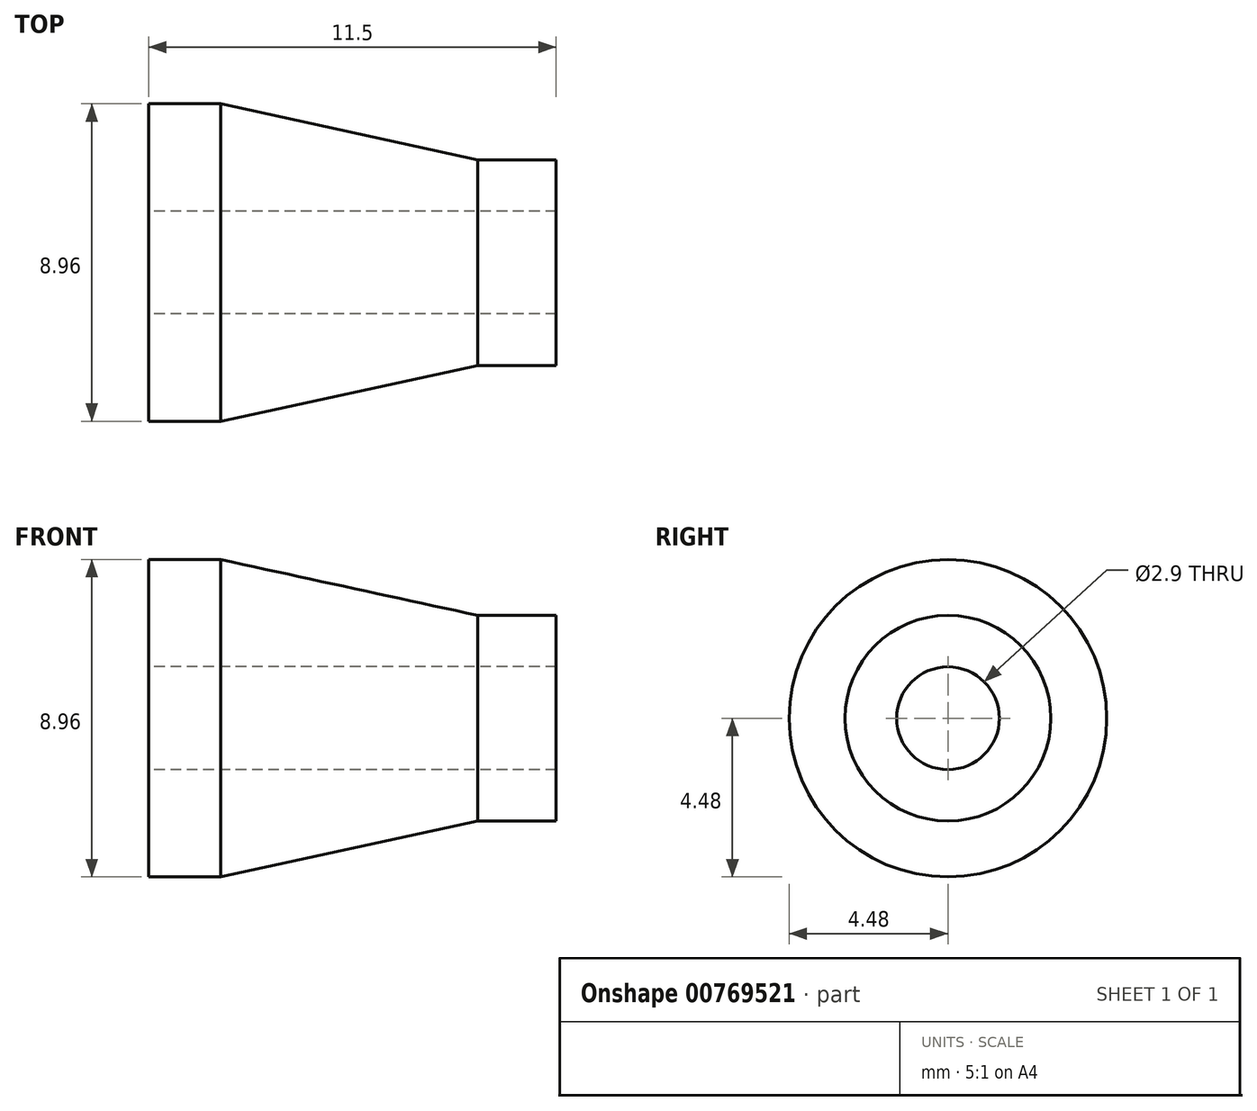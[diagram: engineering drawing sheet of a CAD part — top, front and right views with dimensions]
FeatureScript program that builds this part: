
annotation { "Feature Type Name" : "Feature", "Feature Type Description" : "" }
export const myFeature = defineFeature(function(context is Context, id is Id, definition is map)
    precondition{}
    {
        {
            var Q0;
            Q0=qCreatedBy(makeId("Front.planeOp"),FACE);
            var sketch = newSketch(context, id + "F0", { "sketchPlane" : qUnion([Q0])});
            skLineSegment(sketch, "E0", {"start": v(0, 0) * mm, "end": v(0, 4.48) * mm});
            skLineSegment(sketch, "E1", {"start": v(0, 4.48) * mm, "end": v(2.03, 4.48) * mm});
            skLineSegment(sketch, "E2", {"start": v(2.03, 4.48) * mm, "end": v(2.03, 0) * mm});
            skLineSegment(sketch, "E3", {"start": v(2.03, 4.48) * mm, "end": v(9.3, 2.9) * mm});
            skLineSegment(sketch, "E4", {"start": v(9.3, 2.9) * mm, "end": v(9.3, 0) * mm});
            skLineSegment(sketch, "E5", {"start": v(11.5, 0) * mm, "end": v(11.5, 2.9) * mm});
            skLineSegment(sketch, "E6", {"start": v(9.3, 2.9) * mm, "end": v(11.5, 2.9) * mm});
            skLineSegment(sketch, "E7.trimOffspring", {"start": v(11.5, 0) * mm, "end": v(15.36, 0) * mm, "construction": true});
            skLineSegment(sketch, "E8", {"start": v(0, 0) * mm, "end": v(11.5, 0) * mm});
            skSolve(sketch);
        }
        {
            var Q0;
            Q0 = qSketchRegion(id + "F0", true);
            var Q1;
            Q1=sQuery(id+"F0.wireOp",EDGE,"E8");
            revolve(context, id + "F1", {"surfaceOperationType" : NewSurfaceOperationType.NEW, "entities" : qUnion([Q0]), "axis" : qUnion([Q1]), "revolveType" : RevolveType.FULL});
        }
        {
            var Q0;
            Q0=makeQuery(id+"F1.opRevolve","SWEPT_FACE",FACE,{"disambiguationData":[OSD([sQuery(id+"F0.wireOp",EDGE,"E0")])]});
            var sketch = newSketch(context, id + "F2", { "sketchPlane" : qUnion([Q0])});
            skCircle(sketch, "E9", {"center": v(0, 0) * mm, "radius": 2.3 * mm});
            skCircle(sketch, "E10", {"center": v(0, 0) * mm, "radius": 1.45 * mm});
            skSolve(sketch);
        }
        {
            var Q0;
            Q0=makeQuery(id+"F2.imprint","IMPRINT",FACE,{"disambiguationData":[TD([[makeQuery(id+"F2.imprint","IMPRINT",EDGE,{"derivedFrom":sQuery(id+"F2.wireOp",EDGE,"E10")}),1.0]])]});
            extrude(context, id + "F3", {"entities" : qUnion([Q0]), "operationType" : NewBodyOperationType.REMOVE, "oppositeDirection" : true, "depth" : 25 * mm, "offsetDistance" : 25 * mm});
        }
    });
